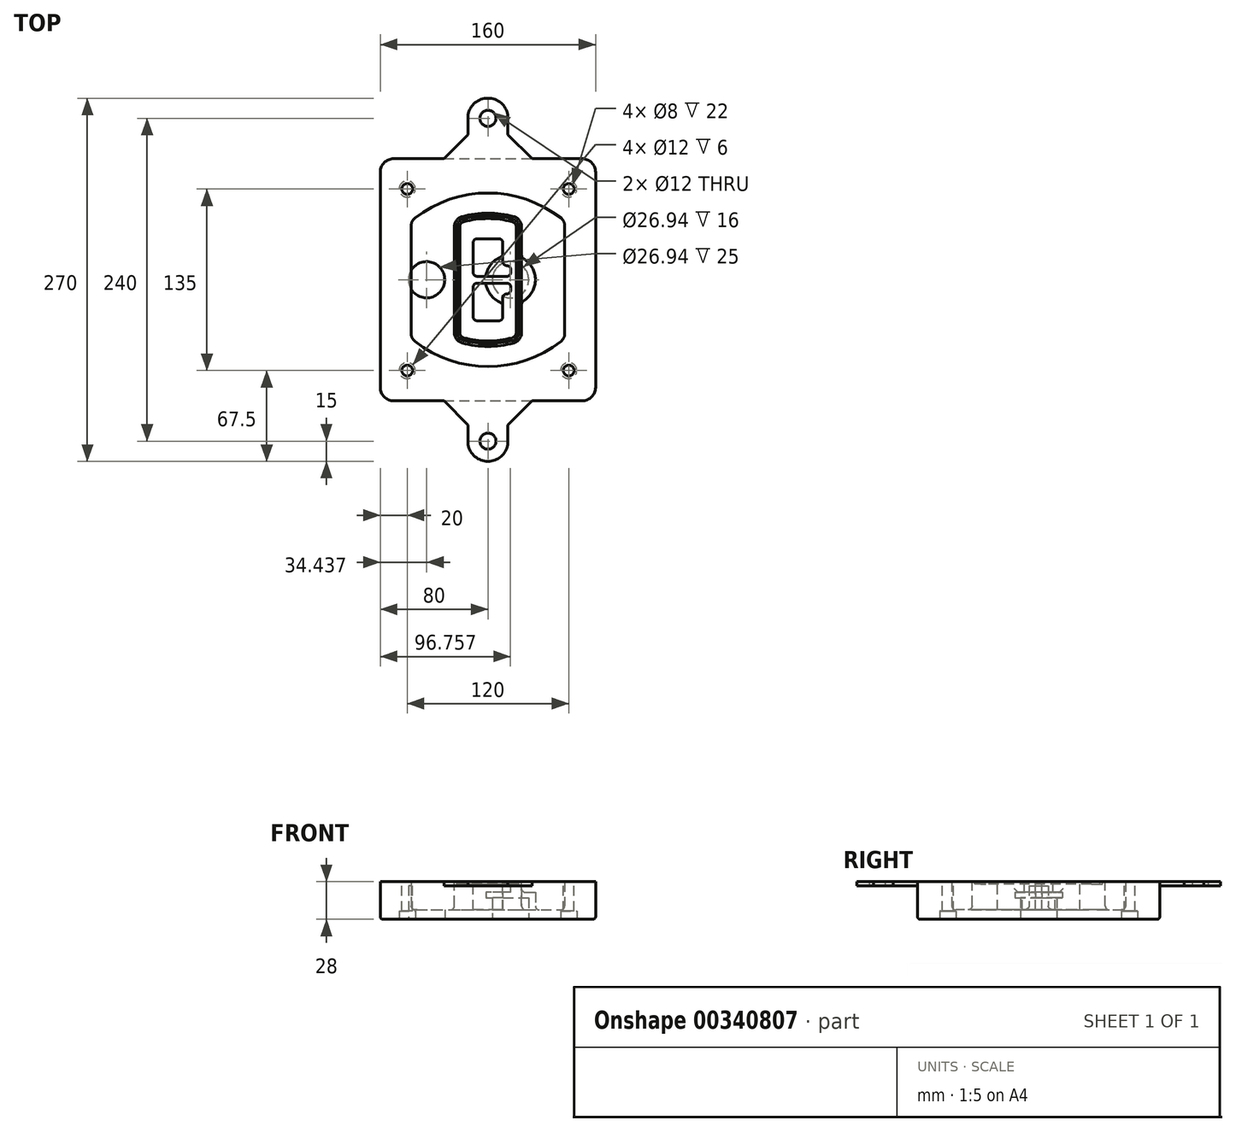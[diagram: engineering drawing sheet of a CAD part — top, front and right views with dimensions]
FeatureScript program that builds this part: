
annotation { "Feature Type Name" : "Feature", "Feature Type Description" : "" }
export const myFeature = defineFeature(function(context is Context, id is Id, definition is map)
    precondition{}
    {
        {
            var Q0;
            Q0=qCreatedBy(makeId("Top.planeOp"),FACE);
            var sketch = newSketch(context, id + "F0", { "sketchPlane" : qUnion([Q0])});
            skPoint(sketch, "E0.rect.middle", {"position": v(0, 0) * mm});
            skLineSegment(sketch, "E1.bottom", {"start": v(-70, -90) * mm, "end": v(70, -90) * mm});
            skLineSegment(sketch, "E1.top", {"start": v(-70, 90) * mm, "end": v(70, 90) * mm});
            skLineSegment(sketch, "E1.left", {"start": v(-80, -80) * mm, "end": v(-80, 80) * mm});
            skLineSegment(sketch, "E1.right", {"start": v(80, -80) * mm, "end": v(80, 80) * mm});
            skLineSegment(sketch, "E2", {"start": v(-80, 90) * mm, "end": v(80, -90) * mm, "construction": true});
            skLineSegment(sketch, "E3", {"start": v(80, 90) * mm, "end": v(-80, -90) * mm, "construction": true});
            skCircle(sketch, "E4", {"center": v(-60, 67.5) * mm, "radius": 4 * mm});
            skCircle(sketch, "E5", {"center": v(60, 67.5) * mm, "radius": 4 * mm});
            skCircle(sketch, "E6", {"center": v(60, -67.5) * mm, "radius": 4 * mm});
            skCircle(sketch, "E7", {"center": v(-60, -67.5) * mm, "radius": 4 * mm});
            skLineSegment(sketch, "E8", {"start": v(-60, 67.5) * mm, "end": v(60, 67.5) * mm, "construction": true});
            skLineSegment(sketch, "E9", {"start": v(60, 67.5) * mm, "end": v(60, -67.5) * mm, "construction": true});
            skLineSegment(sketch, "E10", {"start": v(60, -67.5) * mm, "end": v(-60, -67.5) * mm, "construction": true});
            skLineSegment(sketch, "E11", {"start": v(-60, -67.5) * mm, "end": v(-60, 67.5) * mm, "construction": true});
            skLineSegment(sketch, "E12", {"start": v(-60, 40.3) * mm, "end": v(-60, -40.3) * mm});
            skLineSegment(sketch, "E13", {"start": v(60, 40.3) * mm, "end": v(60, -40.3) * mm});
            skArc(sketch, "E14", {"start": v(56.15, 48.18) * mm, "mid": v(0, 67.5) * mm, "end": v(-56.15, 48.18) * mm});
            skArc(sketch, "E15", {"start": v(-56.15, -48.18) * mm, "mid": v(0, -67.5) * mm, "end": v(56.15, -48.18) * mm});
            skLineSegment(sketch, "E16", {"start": v(-60, 0) * mm, "end": v(60, 0) * mm, "construction": true});
            skPoint(sketch, "E17.visualSharp", {"position": v(-60, -45) * mm});
            skArc(sketch, "E17.filletArc", {"start": v(-60, -40.3) * mm, "mid": v(-58.99, -44.68) * mm, "end": v(-56.15, -48.18) * mm});
            skPoint(sketch, "E18.visualSharp", {"position": v(-60, 45) * mm});
            skArc(sketch, "E18.filletArc", {"start": v(-56.15, 48.18) * mm, "mid": v(-58.99, 44.68) * mm, "end": v(-60, 40.3) * mm});
            skPoint(sketch, "E19.visualSharp", {"position": v(60, 45) * mm});
            skArc(sketch, "E19.filletArc", {"start": v(60, 40.3) * mm, "mid": v(58.99, 44.68) * mm, "end": v(56.15, 48.18) * mm});
            skPoint(sketch, "E20.visualSharp", {"position": v(60, -45) * mm});
            skArc(sketch, "E20.filletArc", {"start": v(56.15, -48.18) * mm, "mid": v(58.99, -44.68) * mm, "end": v(60, -40.3) * mm});
            skPoint(sketch, "E21.visualSharp", {"position": v(-80, 90) * mm});
            skArc(sketch, "E21.filletArc", {"start": v(-70, 90) * mm, "mid": v(-77.07, 87.07) * mm, "end": v(-80, 80) * mm});
            skPoint(sketch, "E22.visualSharp", {"position": v(80, 90) * mm});
            skArc(sketch, "E22.filletArc", {"start": v(80, 80) * mm, "mid": v(77.07, 87.07) * mm, "end": v(70, 90) * mm});
            skPoint(sketch, "E23.visualSharp", {"position": v(80, -90) * mm});
            skArc(sketch, "E23.filletArc", {"start": v(70, -90) * mm, "mid": v(77.07, -87.07) * mm, "end": v(80, -80) * mm});
            skPoint(sketch, "E24.visualSharp", {"position": v(-80, -90) * mm});
            skArc(sketch, "E24.filletArc", {"start": v(-80, -80) * mm, "mid": v(-77.07, -87.07) * mm, "end": v(-70, -90) * mm});
            skArc(sketch, "E25.0", {"start": v(57, 40.3) * mm, "mid": v(56.3, 43.36) * mm, "end": v(54.3, 45.81) * mm});
            skLineSegment(sketch, "E25.1", {"start": v(57, 40.3) * mm, "end": v(57, -40.3) * mm});
            skArc(sketch, "E25.2", {"start": v(54.3, -45.81) * mm, "mid": v(56.3, -43.36) * mm, "end": v(57, -40.3) * mm});
            skArc(sketch, "E25.3", {"start": v(-54.3, -45.81) * mm, "mid": v(0, -64.5) * mm, "end": v(54.3, -45.81) * mm});
            skArc(sketch, "E25.4", {"start": v(-57, -40.3) * mm, "mid": v(-56.3, -43.36) * mm, "end": v(-54.3, -45.81) * mm});
            skArc(sketch, "E25.5", {"start": v(54.3, 45.81) * mm, "mid": v(0, 64.5) * mm, "end": v(-54.3, 45.81) * mm});
            skLineSegment(sketch, "E25.6", {"start": v(-57, 40.3) * mm, "end": v(-57, -40.3) * mm});
            skArc(sketch, "E25.7", {"start": v(-54.3, 45.81) * mm, "mid": v(-56.3, 43.36) * mm, "end": v(-57, 40.3) * mm});
            skArc(sketch, "E26.0", {"start": v(-58.62, 51.33) * mm, "mid": v(-62.58, 46.43) * mm, "end": v(-64, 40.3) * mm});
            skArc(sketch, "E26.1", {"start": v(58.62, 51.33) * mm, "mid": v(0, 71.5) * mm, "end": v(-58.62, 51.33) * mm});
            skArc(sketch, "E26.2", {"start": v(64, 40.3) * mm, "mid": v(62.58, 46.43) * mm, "end": v(58.62, 51.33) * mm});
            skLineSegment(sketch, "E26.3", {"start": v(64, 40.3) * mm, "end": v(64, -40.3) * mm});
            skArc(sketch, "E26.4", {"start": v(58.62, -51.33) * mm, "mid": v(62.58, -46.43) * mm, "end": v(64, -40.3) * mm});
            skLineSegment(sketch, "E26.5", {"start": v(-64, 40.3) * mm, "end": v(-64, -40.3) * mm});
            skArc(sketch, "E26.6", {"start": v(-58.62, -51.33) * mm, "mid": v(0, -71.5) * mm, "end": v(58.62, -51.33) * mm});
            skArc(sketch, "E26.7", {"start": v(-64, -40.3) * mm, "mid": v(-62.58, -46.43) * mm, "end": v(-58.62, -51.33) * mm});
            skSolve(sketch);
        }
        {
            var Q0;
            Q0=makeQuery(id+"F0.imprint","IMPRINT",FACE,{"disambiguationData":[TD([[makeQuery(id+"F0.imprint","IMPRINT",EDGE,{"derivedFrom":sQuery(id+"F0.wireOp",EDGE,"E1.bottom")}),1.0]])]});
            var Q1;
            Q1=makeQuery(id+"F0.imprint","IMPRINT",FACE,{"disambiguationData":[TD([[makeQuery(id+"F0.imprint","IMPRINT",EDGE,{"derivedFrom":sQuery(id+"F0.wireOp",EDGE,"E12")}),1.0]])]});
            var Q2;
            Q2=makeQuery(id+"F0.imprint","IMPRINT",FACE,{"disambiguationData":[TD([[makeQuery(id+"F0.imprint","IMPRINT",EDGE,{"derivedFrom":sQuery(id+"F0.wireOp",EDGE,"E25.0")}),1.0]])]});
            var Q3;
            Q3=makeQuery(id+"F0.imprint","IMPRINT",FACE,{"disambiguationData":[TD([[makeQuery(id+"F0.imprint","IMPRINT",EDGE,{"derivedFrom":sQuery(id+"F0.wireOp",EDGE,"E12")}),-1.0]])]});
            extrude(context, id + "F1", {"entities" : qUnion([Q0, Q1, Q2, Q3]), "oppositeDirection" : true, "depth" : 25 * mm});
        }
        {
            var Q0;
            Q0=makeQuery(id+"F0.imprint","IMPRINT",FACE,{"disambiguationData":[TD([[makeQuery(id+"F0.imprint","IMPRINT",EDGE,{"derivedFrom":sQuery(id+"F0.wireOp",EDGE,"E12")}),1.0]])]});
            extrude(context, id + "F2", {"entities" : qUnion([Q0]), "operationType" : NewBodyOperationType.ADD, "depth" : 3 * mm});
        }
        {
            var Q0;
            Q0=makeQuery(id+"F0.imprint","IMPRINT",FACE,{"disambiguationData":[TD([[makeQuery(id+"F0.imprint","IMPRINT",EDGE,{"derivedFrom":sQuery(id+"F0.wireOp",EDGE,"E25.0")}),1.0]])]});
            extrude(context, id + "F3", {"entities" : qUnion([Q0]), "operationType" : NewBodyOperationType.REMOVE, "oppositeDirection" : true, "depth" : 18 * mm});
        }
        {
            var Q0;
            Q0=makeQuery(id+"F2.opExtrude","CAP_FACE",FACE,{"disambiguationData":[OSD([sQuery(id+"F0.wireOp",EDGE,"E12"),sQuery(id+"F0.wireOp",EDGE,"E13"),sQuery(id+"F0.wireOp",EDGE,"E14"),sQuery(id+"F0.wireOp",EDGE,"E15"),sQuery(id+"F0.wireOp",EDGE,"E17.filletArc"),sQuery(id+"F0.wireOp",EDGE,"E18.filletArc"),sQuery(id+"F0.wireOp",EDGE,"E19.filletArc"),sQuery(id+"F0.wireOp",EDGE,"E20.filletArc"),sQuery(id+"F0.wireOp",EDGE,"E25.0"),sQuery(id+"F0.wireOp",EDGE,"E25.1"),sQuery(id+"F0.wireOp",EDGE,"E25.2"),sQuery(id+"F0.wireOp",EDGE,"E25.3"),sQuery(id+"F0.wireOp",EDGE,"E25.4"),sQuery(id+"F0.wireOp",EDGE,"E25.5"),sQuery(id+"F0.wireOp",EDGE,"E25.6"),sQuery(id+"F0.wireOp",EDGE,"E25.7")])],"isStart":false});
            var sketch = newSketch(context, id + "F4", { "sketchPlane" : qUnion([Q0])});
            skArc(sketch, "E27.0", {"start": v(-19.08, -46.97) * mm, "mid": v(0, -49.5) * mm, "end": v(19.08, -46.97) * mm});
            skArc(sketch, "E28.0", {"start": v(19.08, 46.97) * mm, "mid": v(0, 49.5) * mm, "end": v(-19.08, 46.97) * mm});
            skLineSegment(sketch, "E29", {"start": v(-25, 39.25) * mm, "end": v(-25, -39.25) * mm});
            skLineSegment(sketch, "E30", {"start": v(25, 39.25) * mm, "end": v(25, -39.25) * mm});
            skLineSegment(sketch, "E31", {"start": v(-25, 45.1) * mm, "end": v(25, 45.1) * mm, "construction": true});
            skLineSegment(sketch, "E32", {"start": v(-25, -45.1) * mm, "end": v(25, -45.1) * mm, "construction": true});
            skPoint(sketch, "E33.visualSharp", {"position": v(-25, 45.1) * mm});
            skArc(sketch, "E33.filletArc", {"start": v(-19.08, 46.97) * mm, "mid": v(-23.35, 44.11) * mm, "end": v(-25, 39.25) * mm});
            skPoint(sketch, "E34.visualSharp", {"position": v(25, 45.1) * mm});
            skArc(sketch, "E34.filletArc", {"start": v(25, 39.25) * mm, "mid": v(23.35, 44.11) * mm, "end": v(19.08, 46.97) * mm});
            skPoint(sketch, "E35.visualSharp", {"position": v(25, -45.1) * mm});
            skArc(sketch, "E35.filletArc", {"start": v(19.08, -46.97) * mm, "mid": v(23.35, -44.11) * mm, "end": v(25, -39.25) * mm});
            skPoint(sketch, "E36.visualSharp", {"position": v(-25, -45.1) * mm});
            skArc(sketch, "E36.filletArc", {"start": v(-25, -39.25) * mm, "mid": v(-23.35, -44.11) * mm, "end": v(-19.08, -46.97) * mm});
            skArc(sketch, "E37.0", {"start": v(54.3, 45.81) * mm, "mid": v(0, 64.5) * mm, "end": v(-54.3, 45.81) * mm});
            skArc(sketch, "E37.1", {"start": v(-54.3, 45.81) * mm, "mid": v(-56.3, 43.36) * mm, "end": v(-57, 40.3) * mm});
            skLineSegment(sketch, "E37.2", {"start": v(-57, 40.3) * mm, "end": v(-57, -40.3) * mm});
            skArc(sketch, "E37.3", {"start": v(-57, -40.3) * mm, "mid": v(-56.3, -43.36) * mm, "end": v(-54.3, -45.81) * mm});
            skArc(sketch, "E37.4", {"start": v(-54.3, -45.81) * mm, "mid": v(0, -64.5) * mm, "end": v(54.3, -45.81) * mm});
            skArc(sketch, "E37.5", {"start": v(54.3, -45.81) * mm, "mid": v(56.3, -43.36) * mm, "end": v(57, -40.3) * mm});
            skLineSegment(sketch, "E37.6", {"start": v(57, 40.3) * mm, "end": v(57, -40.3) * mm});
            skArc(sketch, "E37.7", {"start": v(57, 40.3) * mm, "mid": v(56.3, 43.36) * mm, "end": v(54.3, 45.81) * mm});
            skLineSegment(sketch, "E38.0", {"start": v(23, 39.25) * mm, "end": v(23, -39.25) * mm});
            skArc(sketch, "E38.1", {"start": v(18.56, -45.04) * mm, "mid": v(21.76, -42.9) * mm, "end": v(23, -39.25) * mm});
            skArc(sketch, "E38.2", {"start": v(-18.56, -45.04) * mm, "mid": v(0, -47.5) * mm, "end": v(18.56, -45.04) * mm});
            skArc(sketch, "E38.3", {"start": v(-23, -39.25) * mm, "mid": v(-21.76, -42.9) * mm, "end": v(-18.56, -45.04) * mm});
            skLineSegment(sketch, "E38.4", {"start": v(-23, 39.25) * mm, "end": v(-23, -39.25) * mm});
            skArc(sketch, "E38.5", {"start": v(23, 39.25) * mm, "mid": v(21.76, 42.9) * mm, "end": v(18.56, 45.04) * mm});
            skArc(sketch, "E38.6", {"start": v(-18.56, 45.04) * mm, "mid": v(-21.76, 42.9) * mm, "end": v(-23, 39.25) * mm});
            skArc(sketch, "E38.7", {"start": v(18.56, 45.04) * mm, "mid": v(0, 47.5) * mm, "end": v(-18.56, 45.04) * mm});
            skArc(sketch, "E39.0", {"start": v(21, 39.25) * mm, "mid": v(20.18, 41.68) * mm, "end": v(18.04, 43.1) * mm});
            skLineSegment(sketch, "E39.1", {"start": v(21, 39.25) * mm, "end": v(21, -39.25) * mm});
            skArc(sketch, "E39.2", {"start": v(18.04, -43.1) * mm, "mid": v(20.18, -41.68) * mm, "end": v(21, -39.25) * mm});
            skArc(sketch, "E39.3", {"start": v(-18.04, -43.1) * mm, "mid": v(0, -45.5) * mm, "end": v(18.04, -43.1) * mm});
            skArc(sketch, "E39.4", {"start": v(-21, -39.25) * mm, "mid": v(-20.18, -41.68) * mm, "end": v(-18.04, -43.1) * mm});
            skArc(sketch, "E39.5", {"start": v(18.04, 43.1) * mm, "mid": v(0, 45.5) * mm, "end": v(-18.04, 43.1) * mm});
            skLineSegment(sketch, "E39.6", {"start": v(-21, 39.25) * mm, "end": v(-21, -39.25) * mm});
            skArc(sketch, "E39.7", {"start": v(-18.04, 43.1) * mm, "mid": v(-20.18, 41.68) * mm, "end": v(-21, 39.25) * mm});
            skLineSegment(sketch, "E40", {"start": v(-25, 0) * mm, "end": v(25, 0) * mm, "construction": true});
            skLineSegment(sketch, "E41", {"start": v(-11, 5.5) * mm, "end": v(-11, 27.5) * mm});
            skLineSegment(sketch, "E42", {"start": v(-8, 30.5) * mm, "end": v(8, 30.5) * mm});
            skLineSegment(sketch, "E43", {"start": v(11, 27.5) * mm, "end": v(11, 13.5) * mm});
            skLineSegment(sketch, "E44", {"start": v(14, 10.5) * mm, "end": v(14, 10.5) * mm});
            skLineSegment(sketch, "E45", {"start": v(17, 7.5) * mm, "end": v(17, 5.5) * mm});
            skLineSegment(sketch, "E46", {"start": v(14, 2.5) * mm, "end": v(-8, 2.5) * mm});
            skPoint(sketch, "E47.visualSharp", {"position": v(-11, 30.5) * mm});
            skArc(sketch, "E47.filletArc", {"start": v(-8, 30.5) * mm, "mid": v(-10.12, 29.62) * mm, "end": v(-11, 27.5) * mm});
            skPoint(sketch, "E48.visualSharp", {"position": v(11, 30.5) * mm});
            skArc(sketch, "E48.filletArc", {"start": v(11, 27.5) * mm, "mid": v(10.12, 29.62) * mm, "end": v(8, 30.5) * mm});
            skPoint(sketch, "E49.visualSharp", {"position": v(11, 10.5) * mm});
            skArc(sketch, "E49.filletArc", {"start": v(11, 13.5) * mm, "mid": v(11.88, 11.38) * mm, "end": v(14, 10.5) * mm});
            skPoint(sketch, "E50.visualSharp", {"position": v(17, 10.5) * mm});
            skArc(sketch, "E50.filletArc", {"start": v(17, 7.5) * mm, "mid": v(16.12, 9.62) * mm, "end": v(14, 10.5) * mm});
            skPoint(sketch, "E51.visualSharp", {"position": v(17, 2.5) * mm});
            skArc(sketch, "E51.filletArc", {"start": v(14, 2.5) * mm, "mid": v(16.12, 3.38) * mm, "end": v(17, 5.5) * mm});
            skPoint(sketch, "E52.visualSharp", {"position": v(-11, 2.5) * mm});
            skArc(sketch, "E52.filletArc", {"start": v(-11, 5.5) * mm, "mid": v(-10.12, 3.38) * mm, "end": v(-8, 2.5) * mm});
            skLineSegment(sketch, "E53.0.MirrorCS", {"start": v(14, -2.5) * mm, "end": v(-8, -2.5) * mm});
            skArc(sketch, "E54.0.MirrorCS", {"start": v(-11, -5.5) * mm, "mid": v(-10.12, -3.38) * mm, "end": v(-8, -2.5) * mm});
            skLineSegment(sketch, "E55.0.MirrorCS", {"start": v(-11, -5.5) * mm, "end": v(-11, -27.5) * mm});
            skArc(sketch, "E56.0.MirrorCS", {"start": v(-8, -30.5) * mm, "mid": v(-10.12, -29.62) * mm, "end": v(-11, -27.5) * mm});
            skLineSegment(sketch, "E57.0.MirrorCS", {"start": v(-8, -30.5) * mm, "end": v(8, -30.5) * mm});
            skArc(sketch, "E58.0.MirrorCS", {"start": v(11, -27.5) * mm, "mid": v(10.12, -29.62) * mm, "end": v(8, -30.5) * mm});
            skLineSegment(sketch, "E59.0.MirrorCS", {"start": v(11, -27.5) * mm, "end": v(11, -13.5) * mm});
            skArc(sketch, "E60.0.MirrorCS", {"start": v(11, -13.5) * mm, "mid": v(11.88, -11.38) * mm, "end": v(14, -10.5) * mm});
            skArc(sketch, "E61.0.MirrorCS", {"start": v(17, -7.5) * mm, "mid": v(16.12, -9.62) * mm, "end": v(14, -10.5) * mm});
            skLineSegment(sketch, "E62.0.MirrorCS", {"start": v(17, -7.5) * mm, "end": v(17, -5.5) * mm});
            skArc(sketch, "E63.0.MirrorCS", {"start": v(14, -2.5) * mm, "mid": v(16.12, -3.38) * mm, "end": v(17, -5.5) * mm});
            skSolve(sketch);
        }
        {
            var Q0;
            Q0=makeQuery(id+"F4.imprint","IMPRINT",FACE,{"disambiguationData":[TD([[makeQuery(id+"F4.imprint","IMPRINT",EDGE,{"derivedFrom":sQuery(id+"F4.wireOp",EDGE,"E27.0")}),1.0]])]});
            var Q1;
            Q1=makeQuery(id+"F4.imprint","IMPRINT",FACE,{"disambiguationData":[TD([[makeQuery(id+"F4.imprint","IMPRINT",EDGE,{"derivedFrom":sQuery(id+"F4.wireOp",EDGE,"E38.0")}),-1.0]])]});
            var Q2;
            Q2=makeQuery(id+"F4.imprint","IMPRINT",FACE,{"disambiguationData":[TD([[makeQuery(id+"F4.imprint","IMPRINT",EDGE,{"derivedFrom":sQuery(id+"F4.wireOp",EDGE,"E39.0")}),1.0]])]});
            extrude(context, id + "F5", {"entities" : qUnion([Q0, Q1, Q2]), "operationType" : NewBodyOperationType.ADD, "endBound" : BoundingType.UP_TO_NEXT, "oppositeDirection" : true, "depth" : 25 * mm});
        }
        {
            var Q0;
            Q0=makeQuery(id+"F4.imprint","IMPRINT",FACE,{"disambiguationData":[TD([[makeQuery(id+"F4.imprint","IMPRINT",EDGE,{"derivedFrom":sQuery(id+"F4.wireOp",EDGE,"E38.0")}),-1.0]])]});
            extrude(context, id + "F6", {"entities" : qUnion([Q0]), "operationType" : NewBodyOperationType.REMOVE, "oppositeDirection" : true, "depth" : 2 * mm});
        }
        {
            var Q0;
            Q0=makeQuery(id+"F1.opExtrude","CAP_FACE",FACE,{"disambiguationData":[OSD([sQuery(id+"F0.wireOp",EDGE,"E1.bottom"),sQuery(id+"F0.wireOp",EDGE,"E1.top"),sQuery(id+"F0.wireOp",EDGE,"E1.left"),sQuery(id+"F0.wireOp",EDGE,"E1.right"),sQuery(id+"F0.wireOp",EDGE,"E4"),sQuery(id+"F0.wireOp",EDGE,"E5"),sQuery(id+"F0.wireOp",EDGE,"E6"),sQuery(id+"F0.wireOp",EDGE,"E7"),sQuery(id+"F0.wireOp",EDGE,"E21.filletArc"),sQuery(id+"F0.wireOp",EDGE,"E22.filletArc"),sQuery(id+"F0.wireOp",EDGE,"E23.filletArc"),sQuery(id+"F0.wireOp",EDGE,"E24.filletArc")])],"isStart":false});
            var sketch = newSketch(context, id + "F7", { "sketchPlane" : qUnion([Q0])});
            skCircle(sketch, "E64", {"center": v(16.76, 0) * mm, "radius": 13.47 * mm});
            skCircle(sketch, "E65", {"center": v(-45.56, 0) * mm, "radius": 13.47 * mm});
            skLineSegment(sketch, "E66", {"start": v(80, 0) * mm, "end": v(-80, 0) * mm});
            skCircle(sketch, "E67", {"center": v(16.76, 0) * mm, "radius": 18.47 * mm});
            skCircle(sketch, "E68", {"center": v(60, -67.5) * mm, "radius": 6 * mm});
            skCircle(sketch, "E69", {"center": v(-60, -67.5) * mm, "radius": 6 * mm});
            skCircle(sketch, "E70", {"center": v(-60, 67.5) * mm, "radius": 6 * mm});
            skCircle(sketch, "E71", {"center": v(60, 67.5) * mm, "radius": 6 * mm});
            skSolve(sketch);
        }
        {
            var Q0;
            {var subQ1=sQuery(id+"F7.wireOp",EDGE,"E66");var subQ4=sQuery(id+"F7.wireOp",EDGE,"E64");var subQ6=makeQuery(id+"F7.imprint","INTERSECT",VERTEX,{"disambiguationData":[OD(0.0)],"derivedFrom":[subQ4,subQ1]});Q0=makeQuery(id+"F7.imprint","IMPRINT",FACE,{"disambiguationData":[TD([[makeQuery(id+"F7.imprint","IMPRINT",EDGE,{"disambiguationData":[TD([[subQ6,-1.0]])],"derivedFrom":subQ4}),-1.0]])]});}
            var Q1;
            {var subQ0=sQuery(id+"F7.wireOp",EDGE,"E66");var subQ1=sQuery(id+"F7.wireOp",EDGE,"E64");var subQ3=makeQuery(id+"F7.imprint","INTERSECT",VERTEX,{"disambiguationData":[OD(0.0)],"derivedFrom":[subQ1,subQ0]});Q1=makeQuery(id+"F7.imprint","IMPRINT",FACE,{"disambiguationData":[TD([[makeQuery(id+"F7.imprint","IMPRINT",EDGE,{"disambiguationData":[TD([[subQ3,-1.0]])],"derivedFrom":subQ1}),1.0]])]});}
            var Q2;
            {var subQ0=sQuery(id+"F7.wireOp",EDGE,"E66");var subQ1=sQuery(id+"F7.wireOp",EDGE,"E64");var subQ3=makeQuery(id+"F7.imprint","INTERSECT",VERTEX,{"disambiguationData":[OD(0.0)],"derivedFrom":[subQ1,subQ0]});Q2=makeQuery(id+"F7.imprint","IMPRINT",FACE,{"disambiguationData":[TD([[makeQuery(id+"F7.imprint","IMPRINT",EDGE,{"disambiguationData":[TD([[subQ3,1.0]])],"derivedFrom":subQ1}),1.0]])]});}
            var Q3;
            {var subQ1=sQuery(id+"F7.wireOp",EDGE,"E66");var subQ4=sQuery(id+"F7.wireOp",EDGE,"E64");var subQ6=makeQuery(id+"F7.imprint","INTERSECT",VERTEX,{"disambiguationData":[OD(0.0)],"derivedFrom":[subQ4,subQ1]});Q3=makeQuery(id+"F7.imprint","IMPRINT",FACE,{"disambiguationData":[TD([[makeQuery(id+"F7.imprint","IMPRINT",EDGE,{"disambiguationData":[TD([[subQ6,1.0]])],"derivedFrom":subQ4}),-1.0]])]});}
            extrude(context, id + "F8", {"entities" : qUnion([Q0, Q1, Q2, Q3]), "operationType" : NewBodyOperationType.ADD, "oppositeDirection" : true, "depth" : 20 * mm});
        }
        {
            var Q0;
            {var subQ0=sQuery(id+"F7.wireOp",EDGE,"E66");var subQ1=sQuery(id+"F7.wireOp",EDGE,"E64");var subQ3=makeQuery(id+"F7.imprint","INTERSECT",VERTEX,{"disambiguationData":[OD(0.0)],"derivedFrom":[subQ1,subQ0]});Q0=makeQuery(id+"F7.imprint","IMPRINT",FACE,{"disambiguationData":[TD([[makeQuery(id+"F7.imprint","IMPRINT",EDGE,{"disambiguationData":[TD([[subQ3,-1.0]])],"derivedFrom":subQ1}),1.0]])]});}
            var Q1;
            {var subQ0=sQuery(id+"F7.wireOp",EDGE,"E66");var subQ1=sQuery(id+"F7.wireOp",EDGE,"E64");var subQ3=makeQuery(id+"F7.imprint","INTERSECT",VERTEX,{"disambiguationData":[OD(0.0)],"derivedFrom":[subQ1,subQ0]});Q1=makeQuery(id+"F7.imprint","IMPRINT",FACE,{"disambiguationData":[TD([[makeQuery(id+"F7.imprint","IMPRINT",EDGE,{"disambiguationData":[TD([[subQ3,1.0]])],"derivedFrom":subQ1}),1.0]])]});}
            extrude(context, id + "F9", {"entities" : qUnion([Q0, Q1]), "operationType" : NewBodyOperationType.REMOVE, "oppositeDirection" : true, "depth" : 16 * mm});
        }
        {
            var Q0;
            {var subQ0=sQuery(id+"F7.wireOp",EDGE,"E66");var subQ1=sQuery(id+"F7.wireOp",EDGE,"E65");var subQ3=makeQuery(id+"F7.imprint","INTERSECT",VERTEX,{"disambiguationData":[OD(0.0)],"derivedFrom":[subQ1,subQ0]});Q0=makeQuery(id+"F7.imprint","IMPRINT",FACE,{"disambiguationData":[TD([[makeQuery(id+"F7.imprint","IMPRINT",EDGE,{"disambiguationData":[TD([[subQ3,-1.0]])],"derivedFrom":subQ1}),1.0]])]});}
            var Q1;
            {var subQ0=sQuery(id+"F7.wireOp",EDGE,"E66");var subQ1=sQuery(id+"F7.wireOp",EDGE,"E65");var subQ3=makeQuery(id+"F7.imprint","INTERSECT",VERTEX,{"disambiguationData":[OD(0.0)],"derivedFrom":[subQ1,subQ0]});Q1=makeQuery(id+"F7.imprint","IMPRINT",FACE,{"disambiguationData":[TD([[makeQuery(id+"F7.imprint","IMPRINT",EDGE,{"disambiguationData":[TD([[subQ3,1.0]])],"derivedFrom":subQ1}),1.0]])]});}
            extrude(context, id + "F10", {"entities" : qUnion([Q0, Q1]), "operationType" : NewBodyOperationType.REMOVE, "oppositeDirection" : true, "depth" : 25 * mm});
        }
        {
            var Q0;
            Q0=makeQuery(id+"F7.imprint","IMPRINT",FACE,{"disambiguationData":[TD([[makeQuery(id+"F7.imprint","IMPRINT",EDGE,{"derivedFrom":sQuery(id+"F7.wireOp",EDGE,"E68")}),1.0]])]});
            var Q1;
            Q1=makeQuery(id+"F7.imprint","IMPRINT",FACE,{"disambiguationData":[TD([[makeQuery(id+"F7.imprint","IMPRINT",EDGE,{"derivedFrom":makeQuery(id+"F1.opExtrude","CAP_EDGE",EDGE,{"disambiguationData":[OSD([sQuery(id+"F0.wireOp",EDGE,"E5")])],"isStart":false})}),-1.0]])]});
            var Q2;
            Q2=makeQuery(id+"F7.imprint","IMPRINT",FACE,{"disambiguationData":[TD([[makeQuery(id+"F7.imprint","IMPRINT",EDGE,{"derivedFrom":sQuery(id+"F7.wireOp",EDGE,"E69")}),1.0]])]});
            var Q3;
            Q3=makeQuery(id+"F7.imprint","IMPRINT",FACE,{"disambiguationData":[TD([[makeQuery(id+"F7.imprint","IMPRINT",EDGE,{"derivedFrom":makeQuery(id+"F1.opExtrude","CAP_EDGE",EDGE,{"disambiguationData":[OSD([sQuery(id+"F0.wireOp",EDGE,"E4")])],"isStart":false})}),-1.0]])]});
            var Q4;
            Q4=makeQuery(id+"F7.imprint","IMPRINT",FACE,{"disambiguationData":[TD([[makeQuery(id+"F7.imprint","IMPRINT",EDGE,{"derivedFrom":sQuery(id+"F7.wireOp",EDGE,"E70")}),1.0]])]});
            var Q5;
            Q5=makeQuery(id+"F7.imprint","IMPRINT",FACE,{"disambiguationData":[TD([[makeQuery(id+"F7.imprint","IMPRINT",EDGE,{"derivedFrom":makeQuery(id+"F1.opExtrude","CAP_EDGE",EDGE,{"disambiguationData":[OSD([sQuery(id+"F0.wireOp",EDGE,"E7")])],"isStart":false})}),-1.0]])]});
            var Q6;
            Q6=makeQuery(id+"F7.imprint","IMPRINT",FACE,{"disambiguationData":[TD([[makeQuery(id+"F7.imprint","IMPRINT",EDGE,{"derivedFrom":sQuery(id+"F7.wireOp",EDGE,"E71")}),1.0]])]});
            var Q7;
            Q7=makeQuery(id+"F7.imprint","IMPRINT",FACE,{"disambiguationData":[TD([[makeQuery(id+"F7.imprint","IMPRINT",EDGE,{"derivedFrom":makeQuery(id+"F1.opExtrude","CAP_EDGE",EDGE,{"disambiguationData":[OSD([sQuery(id+"F0.wireOp",EDGE,"E6")])],"isStart":false})}),-1.0]])]});
            extrude(context, id + "F11", {"entities" : qUnion([Q0, Q1, Q2, Q3, Q4, Q5, Q6, Q7]), "operationType" : NewBodyOperationType.REMOVE, "oppositeDirection" : true, "depth" : 6 * mm});
        }
        {
            var Q0;
            Q0=makeQuery(id+"F9.boolean.opBoolean","COPY",FACE,{"derivedFrom":makeQuery(id+"F9.opExtrude","CAP_FACE",FACE,{"disambiguationData":[OSD([sQuery(id+"F7.wireOp",EDGE,"E64")])],"isStart":false})});
            var sketch = newSketch(context, id + "F12", { "sketchPlane" : qUnion([Q0])});
            skArc(sketch, "E72.0", {"start": v(11, 17.55) * mm, "mid": v(2.57, 11.82) * mm, "end": v(-1.54, 2.5) * mm});
            skArc(sketch, "E72.1", {"start": v(-1.54, -2.5) * mm, "mid": v(2.57, -11.82) * mm, "end": v(11, -17.55) * mm});
            skLineSegment(sketch, "E73", {"start": v(-1.54, -2.5) * mm, "end": v(14, -2.5) * mm});
            skLineSegment(sketch, "E74.0", {"start": v(14, 2.5) * mm, "end": v(-1.54, 2.5) * mm});
            skArc(sketch, "E74.1", {"start": v(14, 2.5) * mm, "mid": v(16.12, 3.38) * mm, "end": v(17, 5.5) * mm});
            skLineSegment(sketch, "E74.2", {"start": v(17, 7.5) * mm, "end": v(17, 5.5) * mm});
            skArc(sketch, "E74.3", {"start": v(17, 7.5) * mm, "mid": v(16.12, 9.62) * mm, "end": v(14, 10.5) * mm});
            skArc(sketch, "E74.4", {"start": v(11, 13.5) * mm, "mid": v(11.88, 11.38) * mm, "end": v(14, 10.5) * mm});
            skLineSegment(sketch, "E74.5", {"start": v(11, 17.55) * mm, "end": v(11, 13.5) * mm});
            skLineSegment(sketch, "E74.7", {"start": v(14, -2.5) * mm, "end": v(-1.54, -2.5) * mm});
            skArc(sketch, "E74.8", {"start": v(14, -2.5) * mm, "mid": v(16.12, -3.38) * mm, "end": v(17, -5.5) * mm});
            skLineSegment(sketch, "E74.9", {"start": v(17, -7.5) * mm, "end": v(17, -5.5) * mm});
            skArc(sketch, "E74.10", {"start": v(17, -7.5) * mm, "mid": v(16.12, -9.62) * mm, "end": v(14, -10.5) * mm});
            skArc(sketch, "E74.11", {"start": v(11, -13.5) * mm, "mid": v(11.88, -11.38) * mm, "end": v(14, -10.5) * mm});
            skLineSegment(sketch, "E74.12", {"start": v(11, -17.55) * mm, "end": v(11, -13.5) * mm});
            skPoint(sketch, "E75.orphan", {"position": v(11, -27.5) * mm});
            skPoint(sketch, "E76.orphan", {"position": v(-8, -2.5) * mm});
            skPoint(sketch, "E77.orphan", {"position": v(-8, 2.5) * mm});
            skPoint(sketch, "E78.orphan", {"position": v(11, 27.5) * mm});
            skSolve(sketch);
        }
        {
            var Q0;
            {var subQ7=sQuery(id+"F12.wireOp",EDGE,"E72.0");var subQ14=sQuery(id+"F12.wireOp",EDGE,"E72.1");var subQ16=sQuery(id+"F12.wireOp",EDGE,"E74.1");var subQ18=sQuery(id+"F12.wireOp",EDGE,"E74.8");Q0=qUnion([makeQuery(id+"F12.imprint","IMPRINT",FACE,{"disambiguationData":[TD([[makeQuery(id+"F12.imprint","IMPRINT",EDGE,{"derivedFrom":subQ7}),1.0]])]}),makeQuery(id+"F12.imprint","IMPRINT",FACE,{"disambiguationData":[TD([[makeQuery(id+"F12.imprint","IMPRINT",EDGE,{"derivedFrom":subQ14}),1.0]])]}),makeQuery(id+"F12.imprint","IMPRINT",FACE,{"disambiguationData":[TD([[makeQuery(id+"F12.imprint","IMPRINT",EDGE,{"derivedFrom":subQ16}),1.0]])]}),makeQuery(id+"F12.imprint","IMPRINT",FACE,{"disambiguationData":[TD([[makeQuery(id+"F12.imprint","IMPRINT",EDGE,{"derivedFrom":subQ18}),-1.0]])]})]);}
            var Q1;
            Q1=makeQuery(id+"F5.boolean.opBoolean","SPLIT",FACE,{"disambiguationData":[TD([makeQuery(id+"F5.opExtrude","SWEPT_FACE",FACE,{"disambiguationData":[OSD([sQuery(id+"F4.wireOp",EDGE,"E41")])]})])],"derivedFrom":makeQuery(id+"F3.boolean.opBoolean","COPY",FACE,{"derivedFrom":makeQuery(id+"F3.opExtrude","CAP_FACE",FACE,{"disambiguationData":[OSD([sQuery(id+"F0.wireOp",EDGE,"E25.0"),sQuery(id+"F0.wireOp",EDGE,"E25.1"),sQuery(id+"F0.wireOp",EDGE,"E25.2"),sQuery(id+"F0.wireOp",EDGE,"E25.3"),sQuery(id+"F0.wireOp",EDGE,"E25.4"),sQuery(id+"F0.wireOp",EDGE,"E25.5"),sQuery(id+"F0.wireOp",EDGE,"E25.6"),sQuery(id+"F0.wireOp",EDGE,"E25.7")])],"isStart":false})})});
            extrude(context, id + "F13", {"entities" : qUnion([Q0]), "operationType" : NewBodyOperationType.REMOVE, "endBound" : BoundingType.UP_TO_SURFACE, "endBoundEntityFace" : qUnion([Q1]), "depth" : 25 * mm});
        }
        {
            var Q0;
            Q0=makeQuery(id+"F3.boolean.opBoolean","COPY",EDGE,{"derivedFrom":makeQuery(id+"F3.opExtrude","CAP_EDGE",EDGE,{"disambiguationData":[OSD([sQuery(id+"F0.wireOp",EDGE,"E25.6")])],"isStart":false})});
            var Q1;
            Q1=makeQuery(id+"F8.boolean.opBoolean","INTERSECT",EDGE,{"derivedFrom":[makeQuery(id+"F5.opExtrude","SWEPT_FACE",FACE,{"disambiguationData":[OSD([sQuery(id+"F4.wireOp",EDGE,"E30")])]}),makeQuery(id+"F8.opExtrude","CAP_FACE",FACE,{"disambiguationData":[OSD([sQuery(id+"F7.wireOp",EDGE,"E67")])],"isStart":false})]});
            var Q2;
            Q2=makeQuery(id+"F8.boolean.opBoolean","INTERSECT",EDGE,{"disambiguationData":[OD(1.0)],"derivedFrom":[makeQuery(id+"F5.opExtrude","SWEPT_FACE",FACE,{"disambiguationData":[OSD([sQuery(id+"F4.wireOp",EDGE,"E30")])]}),makeQuery(id+"F8.opExtrude","SWEPT_FACE",FACE,{"disambiguationData":[OSD([sQuery(id+"F7.wireOp",EDGE,"E67")])]})]});
            var Q3;
            {var subQ0=sQuery(id+"F4.wireOp",EDGE,"E30");Q3=makeQuery(id+"F8.boolean.opBoolean","SPLIT",EDGE,{"disambiguationData":[TD([makeQuery(id+"F5.opExtrude","SWEPT_FACE",FACE,{"disambiguationData":[OSD([sQuery(id+"F4.wireOp",EDGE,"E35.filletArc")])]})])],"derivedFrom":makeQuery(id+"F5.opExtrude","CAP_EDGE",EDGE,{"disambiguationData":[OSD([subQ0])],"isStart":false})});}
            var Q4;
            {var subQ0=sQuery(id+"F0.wireOp",EDGE,"E25.7");var subQ1=sQuery(id+"F0.wireOp",EDGE,"E25.1");var subQ2=sQuery(id+"F0.wireOp",EDGE,"E25.6");var subQ3=sQuery(id+"F0.wireOp",EDGE,"E25.5");var subQ4=sQuery(id+"F0.wireOp",EDGE,"E25.4");var subQ5=sQuery(id+"F0.wireOp",EDGE,"E25.0");var subQ6=sQuery(id+"F0.wireOp",EDGE,"E25.2");var subQ7=sQuery(id+"F0.wireOp",EDGE,"E25.3");Q4=makeQuery(id+"F8.boolean.opBoolean","INTERSECT",EDGE,{"derivedFrom":[makeQuery(id+"F5.boolean.opBoolean","SPLIT",FACE,{"disambiguationData":[TD([makeQuery(id+"F2.opExtrude","SWEPT_FACE",FACE,{"disambiguationData":[OSD([subQ5])]})])],"derivedFrom":makeQuery(id+"F3.boolean.opBoolean","COPY",FACE,{"derivedFrom":makeQuery(id+"F3.opExtrude","CAP_FACE",FACE,{"disambiguationData":[OSD([subQ5,subQ1,subQ6,subQ7,subQ4,subQ3,subQ2,subQ0])],"isStart":false})})}),makeQuery(id+"F8.opExtrude","SWEPT_FACE",FACE,{"disambiguationData":[OSD([sQuery(id+"F7.wireOp",EDGE,"E67")])]})]});}
            var Q5;
            Q5=makeQuery(id+"F8.boolean.opBoolean","INTERSECT",EDGE,{"disambiguationData":[OD(0.0)],"derivedFrom":[makeQuery(id+"F5.opExtrude","SWEPT_FACE",FACE,{"disambiguationData":[OSD([sQuery(id+"F4.wireOp",EDGE,"E30")])]}),makeQuery(id+"F8.opExtrude","SWEPT_FACE",FACE,{"disambiguationData":[OSD([sQuery(id+"F7.wireOp",EDGE,"E67")])]})]});
            fillet(context, id + "F14", {"entities" : qUnion([Q0, Q1, Q2, Q3, Q4, Q5]), "radius" : 3 * mm, "tangentPropagation" : true, "allowEdgeOverflow" : false});
        }
        {
            var Q0;
            Q0=makeQuery(id+"F1.opExtrude","CAP_EDGE",EDGE,{"disambiguationData":[OSD([sQuery(id+"F0.wireOp",EDGE,"E1.bottom")])],"isStart":false});
            fillet(context, id + "F15", {"entities" : qUnion([Q0]), "radius" : 2 * mm, "tangentPropagation" : true, "allowEdgeOverflow" : false});
        }
        {
            var Q0;
            {var subQ0=sQuery(id+"F0.wireOp",EDGE,"E21.filletArc");var subQ1=sQuery(id+"F0.wireOp",EDGE,"E7");var subQ2=sQuery(id+"F0.wireOp",EDGE,"E6");var subQ3=sQuery(id+"F0.wireOp",EDGE,"E5");var subQ4=sQuery(id+"F0.wireOp",EDGE,"E4");var subQ5=sQuery(id+"F0.wireOp",EDGE,"E22.filletArc");var subQ6=sQuery(id+"F0.wireOp",EDGE,"E1.bottom");var subQ7=sQuery(id+"F0.wireOp",EDGE,"E1.right");var subQ8=sQuery(id+"F0.wireOp",EDGE,"E1.top");var subQ9=sQuery(id+"F0.wireOp",EDGE,"E1.left");var subQ10=sQuery(id+"F0.wireOp",EDGE,"E23.filletArc");var subQ11=sQuery(id+"F0.wireOp",EDGE,"E24.filletArc");Q0=makeQuery(id+"F2.boolean.opBoolean","SPLIT",FACE,{"disambiguationData":[TD([makeQuery(id+"F1.opExtrude","SWEPT_FACE",FACE,{"disambiguationData":[OSD([subQ6])]})])],"derivedFrom":makeQuery(id+"F1.opExtrude","CAP_FACE",FACE,{"disambiguationData":[OSD([subQ6,subQ8,subQ9,subQ7,subQ4,subQ3,subQ2,subQ1,subQ0,subQ5,subQ10,subQ11])],"isStart":true})});}
            var sketch = newSketch(context, id + "F16", { "sketchPlane" : qUnion([Q0])});
            skLineSegment(sketch, "E79.0", {"start": v(-70, 90) * mm, "end": v(70, 90) * mm});
            skLineSegment(sketch, "E79.1", {"start": v(-80, -80) * mm, "end": v(-80, 80) * mm});
            skArc(sketch, "E79.2", {"start": v(-70, 90) * mm, "mid": v(-77.07, 87.07) * mm, "end": v(-80, 80) * mm});
            skArc(sketch, "E79.3", {"start": v(-80, -80) * mm, "mid": v(-77.07, -87.07) * mm, "end": v(-70, -90) * mm});
            skLineSegment(sketch, "E79.4", {"start": v(-70, -90) * mm, "end": v(70, -90) * mm});
            skArc(sketch, "E79.5", {"start": v(70, -90) * mm, "mid": v(77.07, -87.07) * mm, "end": v(80, -80) * mm});
            skLineSegment(sketch, "E79.6", {"start": v(80, -80) * mm, "end": v(80, 80) * mm});
            skLineSegment(sketch, "E79.7", {"start": v(60, 40.3) * mm, "end": v(60, -40.3) * mm});
            skArc(sketch, "E79.8", {"start": v(60, 40.3) * mm, "mid": v(58.99, 44.68) * mm, "end": v(56.15, 48.18) * mm});
            skArc(sketch, "E79.9", {"start": v(80, 80) * mm, "mid": v(77.07, 87.07) * mm, "end": v(70, 90) * mm});
            skArc(sketch, "E79.10", {"start": v(56.15, 48.18) * mm, "mid": v(0, 67.5) * mm, "end": v(-56.15, 48.18) * mm});
            skArc(sketch, "E79.11", {"start": v(-56.15, 48.18) * mm, "mid": v(-58.99, 44.68) * mm, "end": v(-60, 40.3) * mm});
            skLineSegment(sketch, "E79.12", {"start": v(-60, 40.3) * mm, "end": v(-60, -40.3) * mm});
            skArc(sketch, "E79.13", {"start": v(-56.15, -48.18) * mm, "mid": v(0, -67.5) * mm, "end": v(56.15, -48.18) * mm});
            skArc(sketch, "E79.14", {"start": v(-60, -40.3) * mm, "mid": v(-58.99, -44.68) * mm, "end": v(-56.15, -48.18) * mm});
            skArc(sketch, "E79.15", {"start": v(56.15, -48.18) * mm, "mid": v(58.99, -44.68) * mm, "end": v(60, -40.3) * mm});
            skCircle(sketch, "E79.16", {"center": v(60, 67.5) * mm, "radius": 4 * mm});
            skCircle(sketch, "E79.17", {"center": v(-60, 67.5) * mm, "radius": 4 * mm});
            skCircle(sketch, "E79.18", {"center": v(-60, -67.5) * mm, "radius": 4 * mm});
            skCircle(sketch, "E79.19", {"center": v(60, -67.5) * mm, "radius": 4 * mm});
            skLineSegment(sketch, "E80", {"start": v(0, 90) * mm, "end": v(0, 120) * mm, "construction": true});
            skCircle(sketch, "E81", {"center": v(0, 120) * mm, "radius": 6 * mm});
            skLineSegment(sketch, "E82", {"start": v(-32.75, 90) * mm, "end": v(-14.75, 108) * mm});
            skLineSegment(sketch, "E83", {"start": v(-14.75, 108) * mm, "end": v(-14.75, 122.75) * mm});
            skLineSegment(sketch, "E84", {"start": v(32.75, 90) * mm, "end": v(14.75, 108) * mm});
            skLineSegment(sketch, "E85", {"start": v(14.75, 108) * mm, "end": v(14.75, 122.75) * mm});
            skArc(sketch, "E86", {"start": v(14.75, 122.75) * mm, "mid": v(0, 135) * mm, "end": v(-14.75, 122.75) * mm});
            skLineSegment(sketch, "E87.MirrorCS", {"start": v(14.75, 108) * mm, "end": v(0, 108) * mm});
            skPoint(sketch, "E88.endSnap0", {"position": v(80, 0) * mm});
            skLineSegment(sketch, "E89", {"start": v(-80, 0) * mm, "end": v(80, 0) * mm, "construction": true});
            skLineSegment(sketch, "E90.MirrorCS", {"start": v(-32.75, -90) * mm, "end": v(-14.75, -108) * mm});
            skLineSegment(sketch, "E91.MirrorCS", {"start": v(-14.75, -108) * mm, "end": v(-14.75, -122.75) * mm});
            skArc(sketch, "E92.MirrorCS", {"start": v(14.75, -122.75) * mm, "mid": v(0, -135) * mm, "end": v(-14.75, -122.75) * mm});
            skCircle(sketch, "E93.MirrorC", {"center": v(0, -120) * mm, "radius": 6 * mm});
            skLineSegment(sketch, "E94.MirrorCS", {"start": v(14.75, -108) * mm, "end": v(14.75, -122.75) * mm});
            skLineSegment(sketch, "E95.MirrorCS", {"start": v(32.75, -90) * mm, "end": v(14.75, -108) * mm});
            skSolve(sketch);
        }
        {
            var Q0;
            Q0=makeQuery(id+"F16.imprint","IMPRINT",FACE,{"disambiguationData":[TD([[makeQuery(id+"F16.imprint","IMPRINT",EDGE,{"derivedFrom":sQuery(id+"F16.wireOp",EDGE,"E79.1")}),-1.0]])]});
            var Q1;
            Q1=makeQuery(id+"F16.imprint","IMPRINT",FACE,{"disambiguationData":[TD([[makeQuery(id+"F16.imprint","IMPRINT",EDGE,{"derivedFrom":sQuery(id+"F16.wireOp",EDGE,"E81")}),-1.0]])]});
            var Q2;
            {var subQ0=sQuery(id+"F16.wireOp",EDGE,"cc61cd9c-a503-4df2-b188-523457fe0e550.MirrorCS");Q2=makeQuery(id+"F16.imprint","IMPRINT",FACE,{"disambiguationData":[TD([[makeQuery(id+"F16.imprint","IMPRINT",EDGE,{"derivedFrom":subQ0}),1.0]])]});}
            var Q3;
            {var subQ0=sQuery(id+"F16.wireOp",EDGE,"E90.MirrorCS");Q3=makeQuery(id+"F16.imprint","IMPRINT",FACE,{"disambiguationData":[TD([[makeQuery(id+"F16.imprint","IMPRINT",EDGE,{"derivedFrom":subQ0}),1.0]])]});}
            var Q4;
            Q4=makeQuery(id+"F2.opExtrude","CAP_FACE",FACE,{"disambiguationData":[OSD([sQuery(id+"F0.wireOp",EDGE,"E12"),sQuery(id+"F0.wireOp",EDGE,"E13"),sQuery(id+"F0.wireOp",EDGE,"E14"),sQuery(id+"F0.wireOp",EDGE,"E15"),sQuery(id+"F0.wireOp",EDGE,"E17.filletArc"),sQuery(id+"F0.wireOp",EDGE,"E18.filletArc"),sQuery(id+"F0.wireOp",EDGE,"E19.filletArc"),sQuery(id+"F0.wireOp",EDGE,"E20.filletArc"),sQuery(id+"F0.wireOp",EDGE,"E25.0"),sQuery(id+"F0.wireOp",EDGE,"E25.1"),sQuery(id+"F0.wireOp",EDGE,"E25.2"),sQuery(id+"F0.wireOp",EDGE,"E25.3"),sQuery(id+"F0.wireOp",EDGE,"E25.4"),sQuery(id+"F0.wireOp",EDGE,"E25.5"),sQuery(id+"F0.wireOp",EDGE,"E25.6"),sQuery(id+"F0.wireOp",EDGE,"E25.7")])],"isStart":false});
            extrude(context, id + "F17", {"entities" : qUnion([Q0, Q1, Q2, Q3]), "operationType" : NewBodyOperationType.ADD, "endBound" : BoundingType.UP_TO_SURFACE, "endBoundEntityFace" : qUnion([Q4]), "depth" : 25 * mm});
        }
    });
